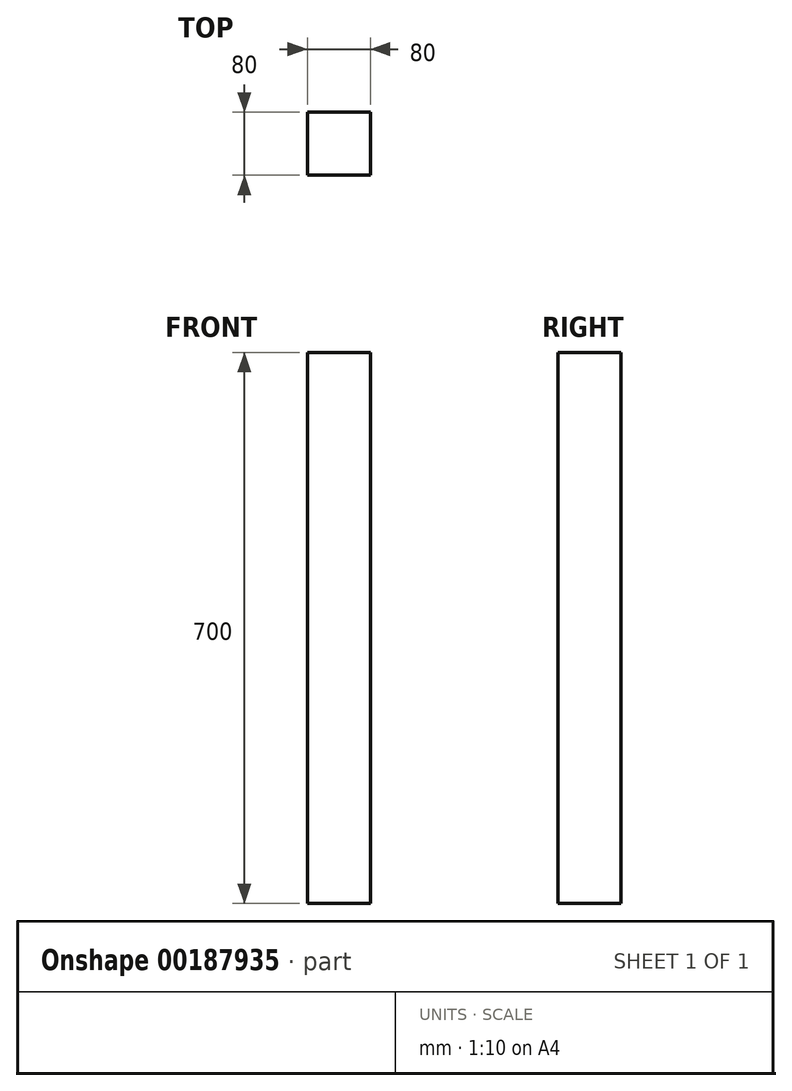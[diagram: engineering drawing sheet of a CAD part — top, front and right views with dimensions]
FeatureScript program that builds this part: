
annotation { "Feature Type Name" : "Feature", "Feature Type Description" : "" }
export const myFeature = defineFeature(function(context is Context, id is Id, definition is map)
    precondition{}
    {
        {
            var Q0;
            Q0=qCreatedBy(makeId("Front.planeOp"),FACE);
            var sketch = newSketch(context, id + "F0", { "sketchPlane" : qUnion([Q0])});
            skLineSegment(sketch, "E0.bottom", {"start": v(0, 521.38) * mm, "end": v(80, 521.38) * mm});
            skLineSegment(sketch, "E0.top", {"start": v(0, -178.62) * mm, "end": v(80, -178.62) * mm});
            skLineSegment(sketch, "E0.left", {"start": v(0, 521.38) * mm, "end": v(0, -178.62) * mm});
            skLineSegment(sketch, "E0.right", {"start": v(80, 521.38) * mm, "end": v(80, -178.62) * mm});
            skSolve(sketch);
        }
        {
            var Q0;
            Q0=makeQuery(id+"F0.imprint","IMPRINT",FACE,{"disambiguationData":[TD([[makeQuery(id+"F0.imprint","IMPRINT",EDGE,{"derivedFrom":sQuery(id+"F0.wireOp",EDGE,"E0.bottom")}),-1.0]])]});
            extrude(context, id + "F1", {"entities" : qUnion([Q0]), "depth" : 80 * mm});
        }
    });
